# Revit family: Table-Teknion-ZNQT_Zones_In_Line_Table-R2022
name_source: partatom
category: Furniture
units: mm (PartAtom-declared; Revit-internal decimal feet)

## family parameters
Always vertical = Yes
Cut with Voids When Loaded = No
Enable Cutting in Views = No
OmniClass Number = 23.40.20.00
OmniClass Title = General Furniture and Specialties
Render Appearance Source = Family Geometry
Room Calculation Point = No
Shared = Yes
Work Plane-Based = No

## types (2) — shared parameters
Assembly Code = E2020200
Manufacturer = Teknion
Manufacturer Fax = 416.661.4586
Part Number = ZNQT
Product Documentation Link = https://www.teknion.com
Product Line = Modular Seating
Product Page URL = https://www.teknion.com
Series = Zones
Sustainability Data = https://www.teknion.com
URL = www.teknion.com
Unit Weight URL = http://www.teknion.com
Warranty = http://www.teknion.com
zero-valued in all types: Default Elevation

## per-type parameters (varying)
| type | Cut-Out - Light | Description | Has Cut-Out | MR - Has Cut-Out | MR - No Cut-Out | Model |
| With Cut Out For Light Style | 3 " | Zones - In-Line Table, With Cut Out For Light Style | Yes | Yes | No | ZNQTY |
| No Cut Out Style | 0.1 " | Zones - In-Line Table, No Cut Out Style | No | No | Yes | ZNQTN |

## geometry (parser evidence)
native form markers: Sweep x3
no freeform markers — native parametric forms only
